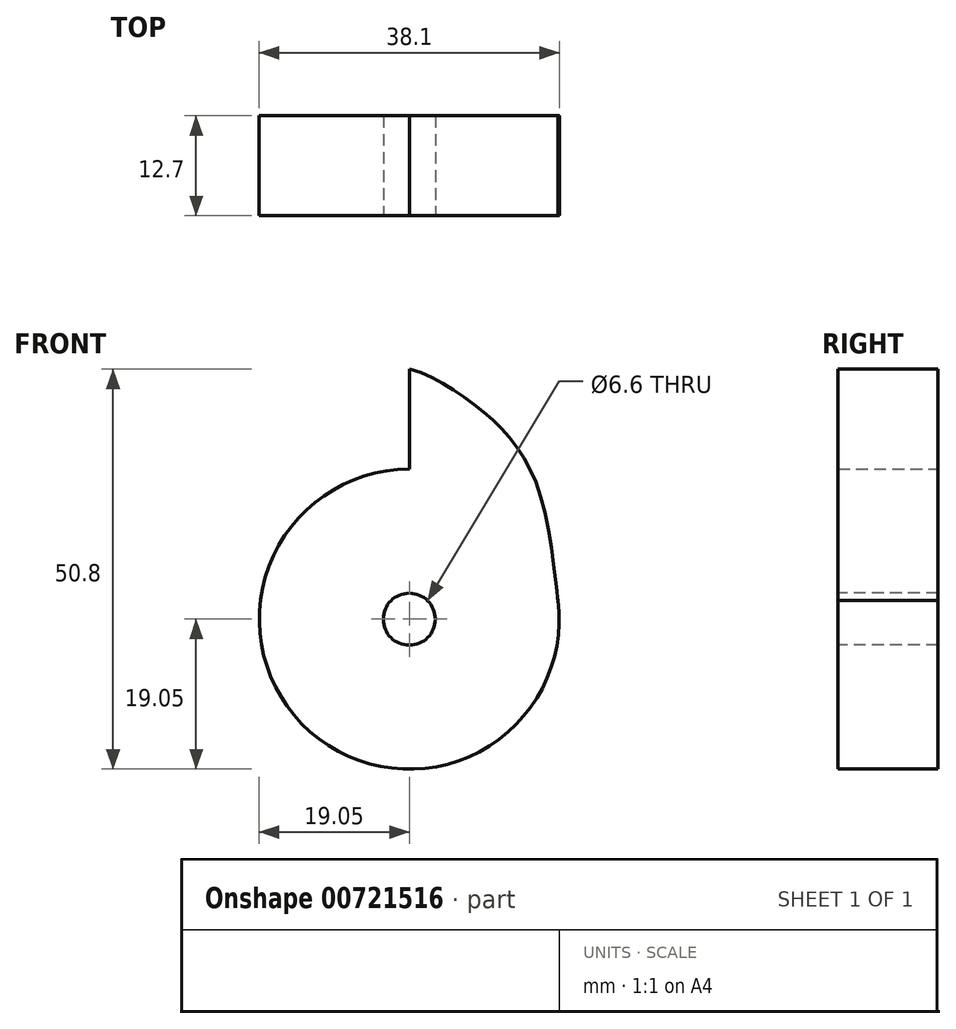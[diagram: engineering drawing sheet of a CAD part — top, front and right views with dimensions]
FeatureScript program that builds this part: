
annotation { "Feature Type Name" : "Feature", "Feature Type Description" : "" }
export const myFeature = defineFeature(function(context is Context, id is Id, definition is map)
    precondition{}
    {
        {
            var Q0;
            Q0=qCreatedBy(makeId("Front.planeOp"),FACE);
            var sketch = newSketch(context, id + "F0", { "sketchPlane" : qUnion([Q0])});
            skCircle(sketch, "E0", {"center": v(0, 0) * mm, "radius": 19.05 * mm});
            skLineSegment(sketch, "E1", {"start": v(0, 19.05) * mm, "end": v(0, 31.75) * mm});
            skFitSpline(sketch, "E2", {"points": [v(0, 31.75) * mm, v(7.08, 28.12) * mm, v(12.87, 22.9) * mm, v(17.12, 14.01) * mm, v(18.85, 2.79) * mm, v(18.9, 2.4) * mm], "startDerivative": vector(34.36, -7.99) * mm, "endDerivative": vector(-0.34, -4.86) * mm});
            skSolve(sketch);
        }
        {
            var Q0;
            Q0 = qSketchRegion(id + "F0", true);
            extrude(context, id + "F1", {"entities" : qUnion([Q0]), "depth" : 12.7 * mm, "offsetDistance" : 25.4 * mm});
        }
        {
            var Q0;
            Q0=makeQuery(id+"F1.opExtrude","CAP_FACE",FACE,{"disambiguationData":[OSD([sQuery(id+"F0.wireOp",EDGE,"E0"),sQuery(id+"F0.wireOp",EDGE,"E1"),sQuery(id+"F0.wireOp",EDGE,"E2")])],"isStart":false});
            var sketch = newSketch(context, id + "F2", { "sketchPlane" : qUnion([Q0])});
            skCircle(sketch, "E3", {"center": v(0, 0) * mm, "radius": 3.3 * mm});
            skSolve(sketch);
        }
        {
            var Q0;
            Q0=makeQuery(id+"F2.imprint","IMPRINT",FACE,{"disambiguationData":[TD([[makeQuery(id+"F2.imprint","IMPRINT",EDGE,{"derivedFrom":sQuery(id+"F2.wireOp",EDGE,"E3")}),1.0]])]});
            extrude(context, id + "F3", {"entities" : qUnion([Q0]), "operationType" : NewBodyOperationType.REMOVE, "oppositeDirection" : true, "depth" : 30.48 * mm, "offsetDistance" : 25.4 * mm});
        }
    });
